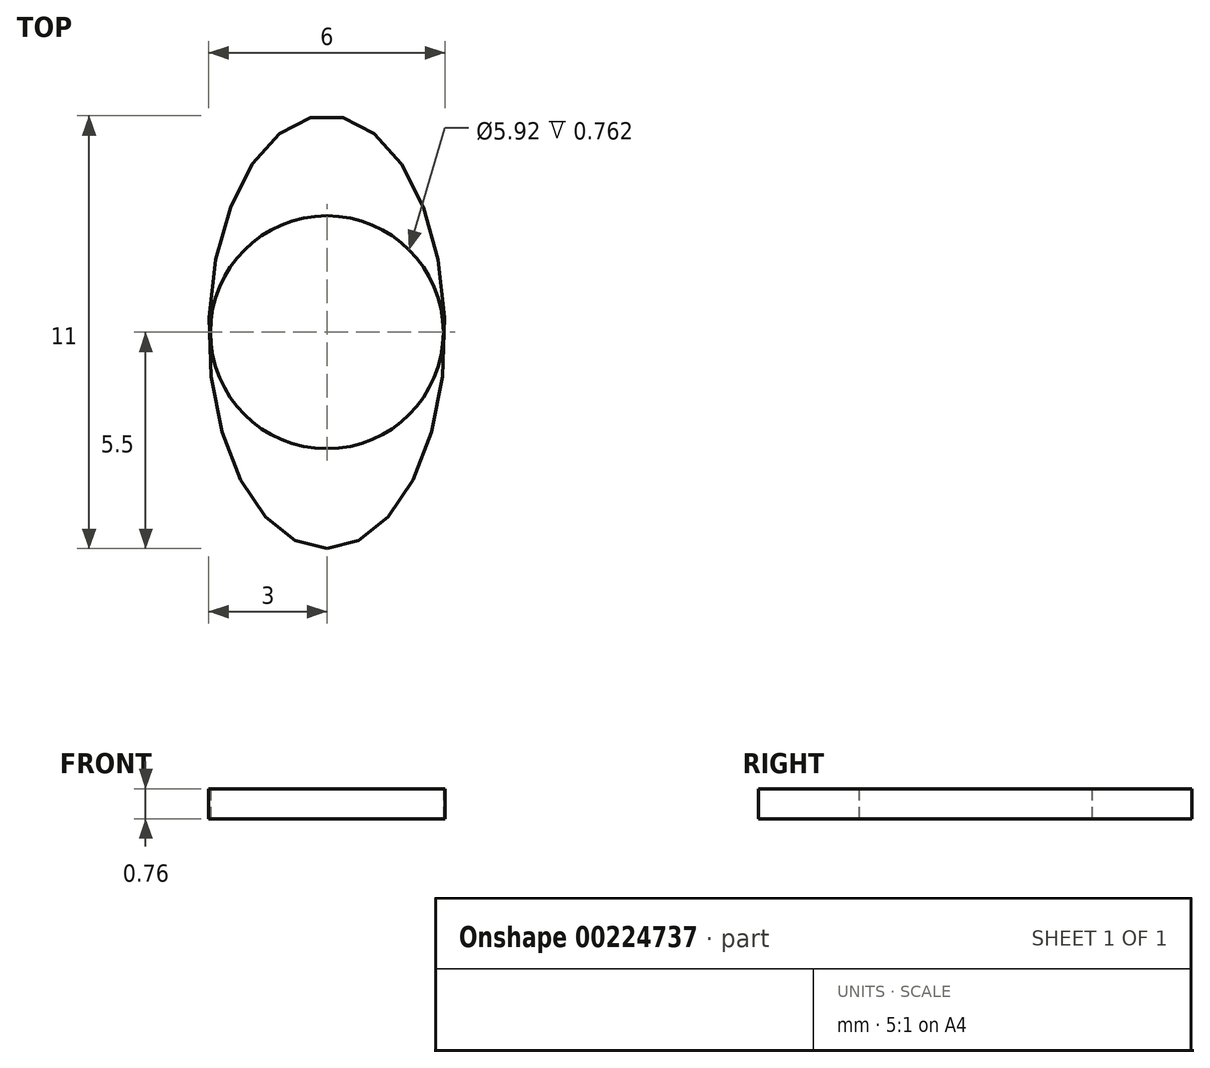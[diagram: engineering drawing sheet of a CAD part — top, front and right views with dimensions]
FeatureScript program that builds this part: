
annotation { "Feature Type Name" : "Feature", "Feature Type Description" : "" }
export const myFeature = defineFeature(function(context is Context, id is Id, definition is map)
    precondition{}
    {
        {
            var Q0;
            Q0=qCreatedBy(makeId("Top.planeOp"),FACE);
            var sketch = newSketch(context, id + "F0", { "sketchPlane" : qUnion([Q0])});
            skCircle(sketch, "E0", {"center": v(0, 0) * mm, "radius": 2.96 * mm});
            skEllipse(sketch, "E1", {"center": v(0, 0) * mm, "majorRadius": 5.5 * mm, "minorRadius": 3 * mm, "majorAxis": v(0, -1)});
            skSolve(sketch);
        }
        {
            var Q0;
            Q0=qSketchRegion(id+"F0",true);
            extrude(context, id + "F1", {"entities" : qUnion([Q0]), "endBound" : BoundingType.SYMMETRIC, "depth" : 0.76 * mm});
        }
    });
